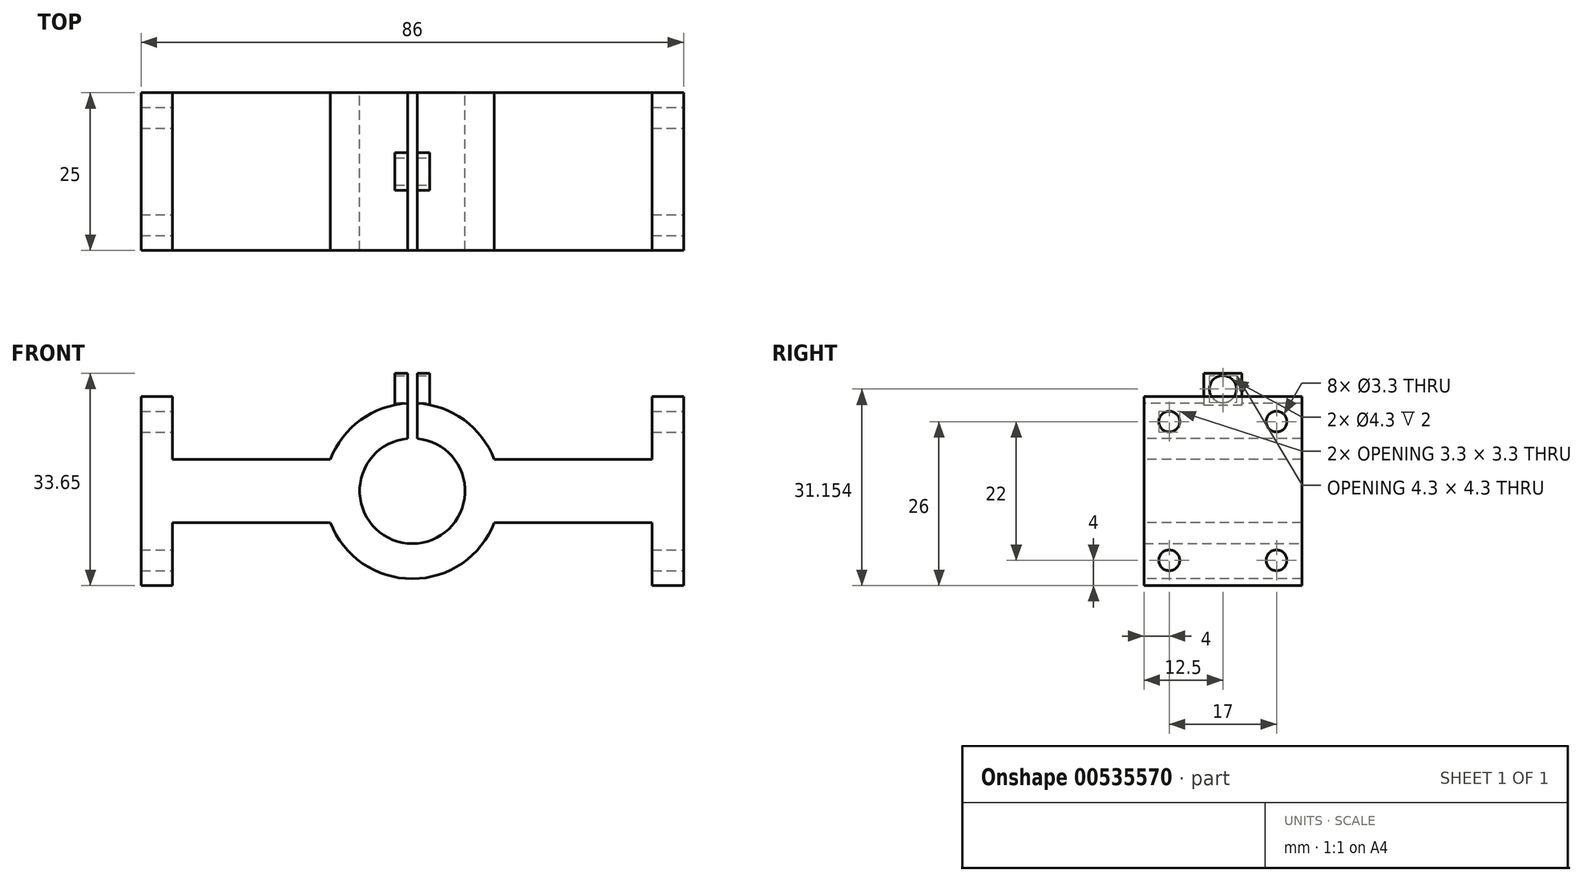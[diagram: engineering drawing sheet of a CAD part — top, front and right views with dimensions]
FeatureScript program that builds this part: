
annotation { "Feature Type Name" : "Feature", "Feature Type Description" : "" }
export const myFeature = defineFeature(function(context is Context, id is Id, definition is map)
    precondition{}
    {
        {
            var Q0;
            Q0=qCreatedBy(makeId("Front.planeOp"),FACE);
            var sketch = newSketch(context, id + "F0", { "sketchPlane" : qUnion([Q0])});
            skCircle(sketch, "E0", {"center": v(0, 0) * mm, "radius": 8.35 * mm});
            skLineSegment(sketch, "E1.bottom", {"start": v(-43, 15) * mm, "end": v(43, 15) * mm});
            skLineSegment(sketch, "E1.top", {"start": v(-43, -15) * mm, "end": v(43, -15) * mm});
            skLineSegment(sketch, "E1.left", {"start": v(-43, 15) * mm, "end": v(-43, -15) * mm});
            skLineSegment(sketch, "E1.right", {"start": v(43, 15) * mm, "end": v(43, -15) * mm});
            skSolve(sketch);
        }
        {
            var Q0;
            Q0 = qSketchRegion(id + "F0", true);
            extrude(context, id + "F1", {"entities" : qUnion([Q0]), "depth" : 25 * mm, "offsetDistance" : 25 * mm, "symmetric" : true});
        }
        {
            var Q0;
            Q0=qCreatedBy(makeId("Front.planeOp"),FACE);
            var sketch = newSketch(context, id + "F2", { "sketchPlane" : qUnion([Q0])});
            skLineSegment(sketch, "E2", {"start": v(-38, 15) * mm, "end": v(-38, 5) * mm});
            skLineSegment(sketch, "E3", {"start": v(-38, 5) * mm, "end": v(-13, 5) * mm});
            skLineSegment(sketch, "E4.MirrorCS", {"start": v(-38, -5) * mm, "end": v(-13, -5) * mm});
            skLineSegment(sketch, "E5.MirrorCS", {"start": v(-38, -15) * mm, "end": v(-38, -5) * mm});
            skLineSegment(sketch, "E6.MirrorCS", {"start": v(38, 15) * mm, "end": v(38, 5) * mm});
            skLineSegment(sketch, "E7.MirrorCS", {"start": v(38, 5) * mm, "end": v(13, 5) * mm});
            skLineSegment(sketch, "E8.MirrorCS", {"start": v(38, -5) * mm, "end": v(13, -5) * mm});
            skLineSegment(sketch, "E9.MirrorCS", {"start": v(38, -15) * mm, "end": v(38, -5) * mm});
            skLineSegment(sketch, "E10", {"start": v(-38, -15) * mm, "end": v(38, -15) * mm});
            skLineSegment(sketch, "E11", {"start": v(38, 15) * mm, "end": v(-38, 15) * mm});
            skArc(sketch, "E12", {"start": v(13, 5) * mm, "mid": v(0, 13.93) * mm, "end": v(-13, 5) * mm});
            skArc(sketch, "E13.MirrorCS", {"start": v(13, -5) * mm, "mid": v(0, -13.93) * mm, "end": v(-13, -5) * mm});
            skSolve(sketch);
        }
        {
            var Q0;
            Q0 = qSketchRegion(id + "F2", true);
            extrude(context, id + "F3", {"entities" : qUnion([Q0]), "operationType" : NewBodyOperationType.REMOVE, "oppositeDirection" : true, "depth" : 25 * mm, "offsetDistance" : 25 * mm, "symmetric" : true});
        }
        {
            var Q0;
            Q0=qCreatedBy(makeId("Right.planeOp"),FACE);
            var sketch = newSketch(context, id + "F4", { "sketchPlane" : qUnion([Q0])});
            skCircle(sketch, "E14", {"center": v(8.5, 11) * mm, "radius": 1.65 * mm});
            skCircle(sketch, "E15.MirrorC", {"center": v(8.5, -11) * mm, "radius": 1.65 * mm});
            skCircle(sketch, "E16.MirrorC", {"center": v(-8.5, 11) * mm, "radius": 1.65 * mm});
            skCircle(sketch, "E17.MirrorC", {"center": v(-8.5, -11) * mm, "radius": 1.65 * mm});
            skSolve(sketch);
        }
        {
            var Q0;
            Q0 = qSketchRegion(id + "F4", true);
            extrude(context, id + "F5", {"entities" : qUnion([Q0]), "operationType" : NewBodyOperationType.REMOVE, "oppositeDirection" : true, "depth" : 130 * mm, "offsetDistance" : 25 * mm, "symmetric" : true});
        }
        {
            var Q0;
            Q0=qCreatedBy(makeId("Right.planeOp"),FACE);
            var sketch = newSketch(context, id + "F6", { "sketchPlane" : qUnion([Q0])});
            skCircle(sketch, "E18", {"center": v(8.5, 11) * mm, "radius": 1.65 * mm});
            skCircle(sketch, "E19.MirrorC", {"center": v(8.5, -11) * mm, "radius": 1.65 * mm});
            skCircle(sketch, "E20.MirrorC", {"center": v(-8.5, 11) * mm, "radius": 1.65 * mm});
            skCircle(sketch, "E21.MirrorC", {"center": v(-8.5, -11) * mm, "radius": 1.65 * mm});
            skSolve(sketch);
        }
        {
            var Q0;
            Q0 = qSketchRegion(id + "F6", true);
            extrude(context, id + "F7", {"entities" : qUnion([Q0]), "operationType" : NewBodyOperationType.ADD, "depth" : 25 * mm, "offsetDistance" : 25 * mm, "symmetric" : true});
        }
        {
            var Q0;
            Q0=qCreatedBy(makeId("Front.planeOp"),FACE);
            var sketch = newSketch(context, id + "F8", { "sketchPlane" : qUnion([Q0])});
            skLineSegment(sketch, "E22", {"start": v(-38, 15) * mm, "end": v(-38, 5) * mm});
            skLineSegment(sketch, "E23", {"start": v(-38, 5) * mm, "end": v(-13, 5) * mm});
            skLineSegment(sketch, "E24.MirrorCS", {"start": v(-38, -5) * mm, "end": v(-13, -5) * mm});
            skLineSegment(sketch, "E25.MirrorCS", {"start": v(-38, -15) * mm, "end": v(-38, -5) * mm});
            skLineSegment(sketch, "E26.MirrorCS", {"start": v(38, 15) * mm, "end": v(38, 5) * mm});
            skLineSegment(sketch, "E27.MirrorCS", {"start": v(38, 5) * mm, "end": v(13, 5) * mm});
            skLineSegment(sketch, "E28.MirrorCS", {"start": v(38, -5) * mm, "end": v(13, -5) * mm});
            skLineSegment(sketch, "E29.MirrorCS", {"start": v(38, -15) * mm, "end": v(38, -5) * mm});
            skLineSegment(sketch, "E30", {"start": v(-38, -15) * mm, "end": v(38, -15) * mm});
            skLineSegment(sketch, "E31", {"start": v(38, 15) * mm, "end": v(-38, 15) * mm});
            skArc(sketch, "E32", {"start": v(13, 5) * mm, "mid": v(0, 13.93) * mm, "end": v(-13, 5) * mm});
            skArc(sketch, "E33.MirrorCS", {"start": v(13, -5) * mm, "mid": v(0, -13.93) * mm, "end": v(-13, -5) * mm});
            skSolve(sketch);
        }
        {
            var Q0;
            Q0 = qSketchRegion(id + "F8", true);
            extrude(context, id + "F9", {"entities" : qUnion([Q0]), "operationType" : NewBodyOperationType.REMOVE, "oppositeDirection" : true, "depth" : 25 * mm, "offsetDistance" : 25 * mm, "symmetric" : true});
        }
        {
            var Q0;
            Q0=qCreatedBy(makeId("Front.planeOp"),FACE);
            var sketch = newSketch(context, id + "F10", { "sketchPlane" : qUnion([Q0])});
            skLineSegment(sketch, "E34", {"start": v(-0.75, 13.9) * mm, "end": v(-0.75, 8.32) * mm});
            skLineSegment(sketch, "E35.MirrorCS", {"start": v(0.75, 13.9) * mm, "end": v(0.75, 8.32) * mm});
            skArc(sketch, "E36", {"start": v(0.75, 13.9) * mm, "mid": v(0, 14.66) * mm, "end": v(-0.75, 13.9) * mm});
            skArc(sketch, "E37", {"start": v(-0.75, 8.32) * mm, "mid": v(0, 7.57) * mm, "end": v(0.75, 8.32) * mm});
            skSolve(sketch);
        }
        {
            var Q0;
            Q0 = qSketchRegion(id + "F10", true);
            extrude(context, id + "F11", {"entities" : qUnion([Q0]), "operationType" : NewBodyOperationType.REMOVE, "oppositeDirection" : true, "depth" : 25 * mm, "offsetDistance" : 25 * mm, "symmetric" : true});
        }
        {
            var Q0;
            Q0=qCreatedBy(makeId("Front.planeOp"),FACE);
            var sketch = newSketch(context, id + "F12", { "sketchPlane" : qUnion([Q0])});
            skLineSegment(sketch, "E38", {"start": v(-0.75, 18.65) * mm, "end": v(-0.75, 13.9) * mm});
            skLineSegment(sketch, "E39", {"start": v(-0.75, 18.65) * mm, "end": v(-2.75, 18.65) * mm});
            skLineSegment(sketch, "E40", {"start": v(-2.75, 18.65) * mm, "end": v(-2.75, 13.65) * mm});
            skArc(sketch, "E41", {"start": v(-0.75, 13.9) * mm, "mid": v(-1.75, 13.82) * mm, "end": v(-2.75, 13.65) * mm});
            skArc(sketch, "E42.MirrorCS", {"start": v(0.75, 13.9) * mm, "mid": v(1.75, 13.82) * mm, "end": v(2.75, 13.65) * mm});
            skLineSegment(sketch, "E43.MirrorCS", {"start": v(0.75, 18.65) * mm, "end": v(0.75, 13.9) * mm});
            skLineSegment(sketch, "E44.MirrorCS", {"start": v(2.75, 18.65) * mm, "end": v(2.75, 13.65) * mm});
            skLineSegment(sketch, "E45.MirrorCS", {"start": v(0.75, 18.65) * mm, "end": v(2.75, 18.65) * mm});
            skSolve(sketch);
        }
        {
            var Q0;
            Q0 = qSketchRegion(id + "F12", true);
            extrude(context, id + "F13", {"entities" : qUnion([Q0]), "operationType" : NewBodyOperationType.ADD, "depth" : 6 * mm, "offsetDistance" : 25 * mm, "symmetric" : true});
        }
        {
            var Q0;
            Q0=qCreatedBy(makeId("Right.planeOp"),FACE);
            var sketch = newSketch(context, id + "F14", { "sketchPlane" : qUnion([Q0])});
            skCircle(sketch, "E46", {"center": v(0, 16.15) * mm, "radius": 2.15 * mm});
            skSolve(sketch);
        }
        {
            var Q0;
            Q0 = qSketchRegion(id + "F14", true);
            extrude(context, id + "F15", {"entities" : qUnion([Q0]), "operationType" : NewBodyOperationType.REMOVE, "oppositeDirection" : true, "depth" : 25 * mm, "offsetDistance" : 25 * mm, "symmetric" : true});
        }
    });
